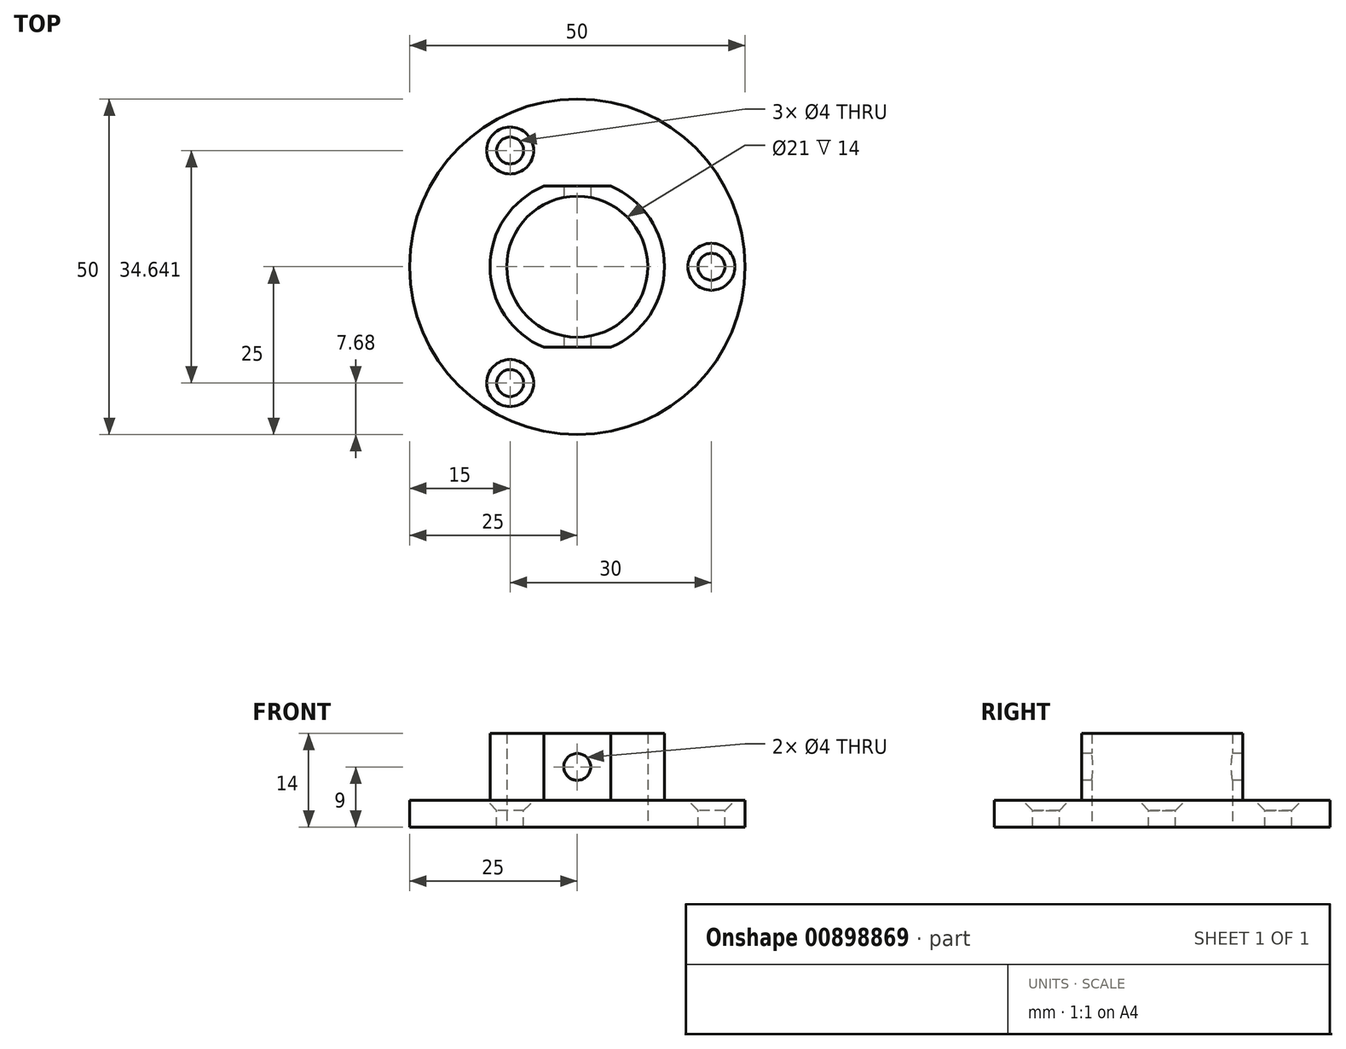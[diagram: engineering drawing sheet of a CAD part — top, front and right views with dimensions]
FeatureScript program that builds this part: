
annotation { "Feature Type Name" : "Feature", "Feature Type Description" : "" }
export const myFeature = defineFeature(function(context is Context, id is Id, definition is map)
    precondition{}
    {
        {
            var Q0;
            Q0=qCreatedBy(makeId("Top.planeOp"),FACE);
            var sketch = newSketch(context, id + "F0", { "sketchPlane" : qUnion([Q0])});
            skCircle(sketch, "E0", {"center": v(0, 0) * mm, "radius": 10.5 * mm});
            skCircle(sketch, "E1", {"center": v(0, 0) * mm, "radius": 25 * mm});
            skSolve(sketch);
        }
        {
            var Q0;
            Q0=makeQuery(id+"F0.imprint","IMPRINT",FACE,{"disambiguationData":[TD([[makeQuery(id+"F0.imprint","IMPRINT",EDGE,{"derivedFrom":sQuery(id+"F0.wireOp",EDGE,"E0")}),-1.0]])]});
            extrude(context, id + "F1", {"entities" : qUnion([Q0]), "depth" : 4 * mm, "offsetDistance" : 25 * mm});
        }
        {
            var Q0;
            Q0=makeQuery(id+"F1.opExtrude","CAP_FACE",FACE,{"disambiguationData":[OSD([sQuery(id+"F0.wireOp",EDGE,"E0"),sQuery(id+"F0.wireOp",EDGE,"E1")])],"isStart":false});
            var sketch = newSketch(context, id + "F2", { "sketchPlane" : qUnion([Q0])});
            skArc(sketch, "E2", {"start": v(5, -12) * mm, "mid": v(13, 0) * mm, "end": v(5, 12) * mm});
            skLineSegment(sketch, "E3.bottom", {"start": v(5, 12) * mm, "end": v(-5, 12) * mm});
            skLineSegment(sketch, "E3.top", {"start": v(5, -12) * mm, "end": v(-5, -12) * mm});
            skArc(sketch, "E4.trimOffspring", {"start": v(-5, 12) * mm, "mid": v(-13, 0) * mm, "end": v(-5, -12) * mm});
            skPoint(sketch, "E3.right.end.orphan", {"position": v(-18.76, -12) * mm});
            skPoint(sketch, "E3.right.start.orphan", {"position": v(-17.98, 12) * mm});
            skPoint(sketch, "E3.left.end.orphan", {"position": v(17.98, -12) * mm});
            skPoint(sketch, "E3.left.start.orphan", {"position": v(18.76, 12) * mm});
            skSolve(sketch);
        }
        {
            var Q0;
            Q0=makeQuery(id+"F2.imprint","IMPRINT",FACE,{"disambiguationData":[TD([[makeQuery(id+"F2.imprint","IMPRINT",EDGE,{"derivedFrom":sQuery(id+"F2.wireOp",EDGE,"E2")}),1.0]])]});
            extrude(context, id + "F3", {"entities" : qUnion([Q0]), "operationType" : NewBodyOperationType.ADD, "depth" : 10 * mm, "offsetDistance" : 25 * mm});
        }
        {
            var Q0;
            Q0=makeQuery(id+"F1.opExtrude","CAP_FACE",FACE,{"disambiguationData":[OSD([sQuery(id+"F0.wireOp",EDGE,"E0"),sQuery(id+"F0.wireOp",EDGE,"E1")])],"isStart":false});
            var sketch = newSketch(context, id + "F4", { "sketchPlane" : qUnion([Q0])});
            skLineSegment(sketch, "E5", {"start": v(0, 0) * mm, "end": v(20, 0) * mm, "construction": true});
            skPoint(sketch, "E5.endSnap0", {"position": v(13, 0) * mm});
            skLineSegment(sketch, "E6", {"start": v(0, 0) * mm, "end": v(-10, 17.32) * mm, "construction": true});
            skLineSegment(sketch, "E7", {"start": v(0, 0) * mm, "end": v(-10, -17.32) * mm, "construction": true});
            skCircle(sketch, "E8", {"center": v(0, 0) * mm, "radius": 20 * mm, "construction": true});
            skPoint(sketch, "E9.orphan", {"position": v(20, 0) * mm});
            skSolve(sketch);
        }
        {
            var Q0;
            Q0=sQuery(id+"F4.wireOp",VERTEX,"E7.end");
            var Q1;
            Q1=sQuery(id+"F4.wireOp",VERTEX,"E6.end");
            var Q2;
            Q2=sQuery(id+"F4.wireOp",VERTEX,"E9.orphan");
            var Q3;
            Q3=makeQuery(id+"F1.opExtrude","SWEPT_BODY",BODY,{"disambiguationData":[OSD([sQuery(id+"F0.wireOp",EDGE,"E0"),sQuery(id+"F0.wireOp",EDGE,"E1")])]});
            hole(context, id + "F5", {"style" : HoleStyle.C_SINK, "endStyle" : HoleEndStyle.THROUGH, "holeDiameter" : 4 * mm, "cSinkDiameter" : 7 * mm, "cSinkAngle" : 90 * degree, "majorDiameter" : 5 * mm, "isTappedThrough" : true, "tappedDepth" : 12 * mm, "tapClearance" : 3, "locations" : qUnion([Q0, Q1, Q2]), "scope" : qUnion([Q3])});
        }
        {
            var Q0;
            Q0=makeQuery(id+"F3.opExtrude","SWEPT_FACE",FACE,{"disambiguationData":[OSD([sQuery(id+"F2.wireOp",EDGE,"E3.top")])]});
            var sketch = newSketch(context, id + "F6", { "sketchPlane" : qUnion([Q0])});
            skPoint(sketch, "E10", {"position": v(0, 9) * mm});
            skPoint(sketch, "E10.positionSnap0", {"position": v(0, 14) * mm});
            skSolve(sketch);
        }
        {
            var Q0;
            Q0=sQuery(id+"F6.wireOp",VERTEX,"E10");
            var Q1;
            Q1=makeQuery(id+"F1.opExtrude","SWEPT_BODY",BODY,{"disambiguationData":[OSD([sQuery(id+"F0.wireOp",EDGE,"E0"),sQuery(id+"F0.wireOp",EDGE,"E1")])]});
            hole(context, id + "F7", {"style" : HoleStyle.SIMPLE, "endStyle" : HoleEndStyle.THROUGH, "holeDiameter" : 4 * mm, "majorDiameter" : 5 * mm, "isTappedThrough" : true, "tappedDepth" : 12 * mm, "tapClearance" : 3, "locations" : qUnion([Q0]), "scope" : qUnion([Q1])});
        }
    });
